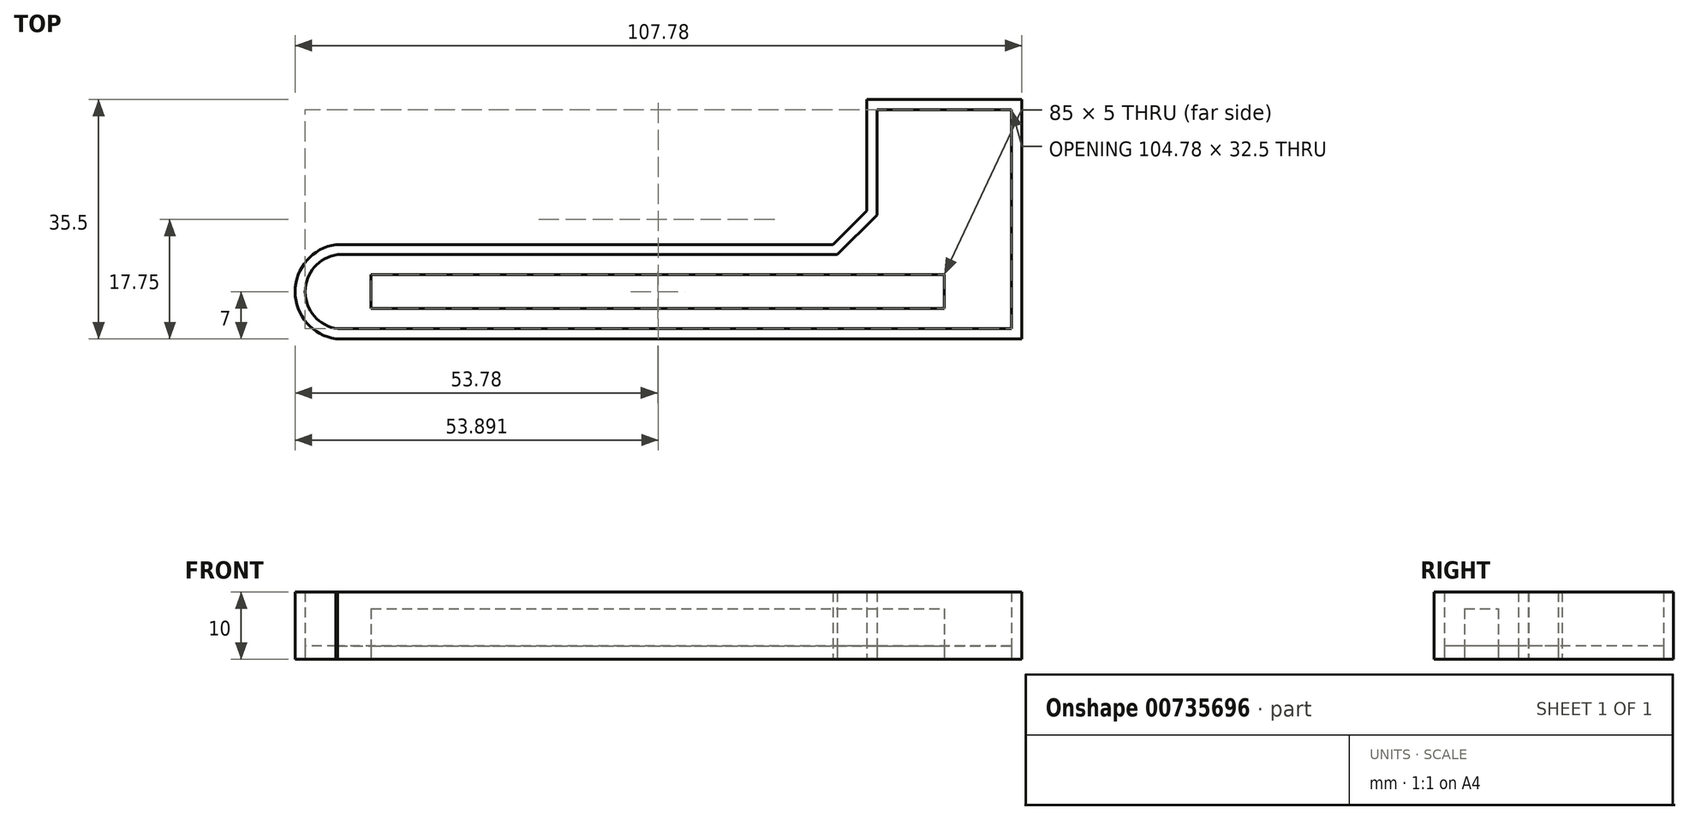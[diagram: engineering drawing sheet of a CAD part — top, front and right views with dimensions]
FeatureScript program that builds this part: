
annotation { "Feature Type Name" : "Feature", "Feature Type Description" : "" }
export const myFeature = defineFeature(function(context is Context, id is Id, definition is map)
    precondition{}
    {
        {
            var Q0;
            Q0=qCreatedBy(makeId("Top.planeOp"),FACE);
            var sketch = newSketch(context, id + "F0", { "sketchPlane" : qUnion([Q0])});
            skLineSegment(sketch, "E0", {"start": v(-133.1, 0.86) * mm, "end": v(-138.1, 0.86) * mm});
            skLineSegment(sketch, "E1", {"start": v(-133.1, 11.86) * mm, "end": v(-138.1, 11.86) * mm});
            skArc(sketch, "E2", {"start": v(-138.1, 11.86) * mm, "mid": v(-142.89, 6.36) * mm, "end": v(-138.1, 0.86) * mm});
            skArc(sketch, "E3.0", {"start": v(-138.32, 13.35) * mm, "mid": v(-144.39, 6.36) * mm, "end": v(-138.32, -0.63) * mm});
            skLineSegment(sketch, "E4", {"start": v(-138.32, 13.35) * mm, "end": v(-138.1, 13.36) * mm});
            skLineSegment(sketch, "E5", {"start": v(-138.1, -0.64) * mm, "end": v(-138.32, -0.63) * mm});
            skLineSegment(sketch, "E6", {"start": v(-48.1, 33.36) * mm, "end": v(-58.1, 33.36) * mm});
            skLineSegment(sketch, "E7", {"start": v(-58.1, 33.36) * mm, "end": v(-38.1, 33.36) * mm});
            skLineSegment(sketch, "E8.left", {"start": v(-58.1, 33.36) * mm, "end": v(-58.1, 23.36) * mm});
            skLineSegment(sketch, "E9.0", {"start": v(-59.6, 33.36) * mm, "end": v(-59.6, 23.98) * mm});
            skLineSegment(sketch, "E10.0", {"start": v(-58.1, 34.86) * mm, "end": v(-38.1, 34.86) * mm});
            skLineSegment(sketch, "E11.0", {"start": v(-36.6, 33.36) * mm, "end": v(-36.6, 23.98) * mm});
            skLineSegment(sketch, "E12", {"start": v(-59.6, 33.36) * mm, "end": v(-59.6, 34.86) * mm});
            skLineSegment(sketch, "E13", {"start": v(-59.6, 34.86) * mm, "end": v(-58.1, 34.86) * mm});
            skLineSegment(sketch, "E14", {"start": v(-38.1, 34.86) * mm, "end": v(-36.6, 34.86) * mm});
            skLineSegment(sketch, "E15", {"start": v(-36.6, 34.86) * mm, "end": v(-36.6, 33.36) * mm});
            skPoint(sketch, "E16.orphan", {"position": v(-38.1, 23.36) * mm});
            skPoint(sketch, "E8.top.start.orphan", {"position": v(-58.1, 13.36) * mm});
            skPoint(sketch, "E17.orphan", {"position": v(-38.1, 13.36) * mm});
            skLineSegment(sketch, "E18.trimOffspring", {"start": v(-69.6, 11.86) * mm, "end": v(-138.1, 11.86) * mm});
            skLineSegment(sketch, "E19.trimOffspring", {"start": v(-70.23, 13.36) * mm, "end": v(-138.1, 13.36) * mm});
            skPoint(sketch, "E20.end.orphan", {"position": v(-48.1, 13.36) * mm});
            skPoint(sketch, "E21.start.orphan", {"position": v(-48.1, 8.86) * mm});
            skLineSegment(sketch, "E22", {"start": v(-70.23, 13.36) * mm, "end": v(-64.6, 13.36) * mm});
            skLineSegment(sketch, "E23", {"start": v(-59.6, 18.36) * mm, "end": v(-59.6, 23.98) * mm});
            skLineSegment(sketch, "E24", {"start": v(-64.6, 13.36) * mm, "end": v(-64.92, 13.36) * mm});
            skLineSegment(sketch, "E25", {"start": v(-59.6, 18.36) * mm, "end": v(-64.6, 13.36) * mm});
            skLineSegment(sketch, "E26.0", {"start": v(-58.55, 17.3) * mm, "end": v(-63.55, 12.3) * mm});
            skLineSegment(sketch, "E27", {"start": v(-69.6, 11.86) * mm, "end": v(-63.99, 11.86) * mm});
            skLineSegment(sketch, "E28", {"start": v(-63.55, 12.3) * mm, "end": v(-63.99, 11.86) * mm});
            skLineSegment(sketch, "E29", {"start": v(-58.1, 23.36) * mm, "end": v(-58.1, 17.74) * mm});
            skLineSegment(sketch, "E30", {"start": v(-58.55, 17.3) * mm, "end": v(-58.1, 17.74) * mm});
            skPoint(sketch, "E31.orphan", {"position": v(-59.6, 13.36) * mm});
            skLineSegment(sketch, "E32.MirrorCS", {"start": v(-36.6, 33.36) * mm, "end": v(-36.6, 34.86) * mm});
            skLineSegment(sketch, "E33.MirrorCS", {"start": v(-36.6, 34.86) * mm, "end": v(-38.1, 34.86) * mm});
            skLineSegment(sketch, "E34.MirrorCS", {"start": v(-36.6, 18.36) * mm, "end": v(-36.6, 23.98) * mm});
            skPoint(sketch, "E35.MirrorP", {"position": v(-36.6, 13.36) * mm});
            skLineSegment(sketch, "E36", {"start": v(-137.33, 6.36) * mm, "end": v(-133.1, 6.36) * mm, "construction": true});
            skLineSegment(sketch, "E37", {"start": v(-133.1, 6.36) * mm, "end": v(-133.1, 3.86) * mm});
            skLineSegment(sketch, "E38", {"start": v(-133.1, 3.86) * mm, "end": v(-48.1, 3.86) * mm});
            skLineSegment(sketch, "E39", {"start": v(-138.1, -0.64) * mm, "end": v(-36.6, -0.64) * mm});
            skLineSegment(sketch, "E40", {"start": v(-36.6, -0.64) * mm, "end": v(-36.6, 18.36) * mm});
            skLineSegment(sketch, "E41", {"start": v(-133.1, 6.36) * mm, "end": v(-133.1, 8.86) * mm});
            skLineSegment(sketch, "E42", {"start": v(-133.1, 8.86) * mm, "end": v(-48.1, 8.86) * mm});
            skLineSegment(sketch, "E43", {"start": v(-48.1, 8.86) * mm, "end": v(-48.1, 3.86) * mm});
            skLineSegment(sketch, "E44", {"start": v(-38.1, 33.36) * mm, "end": v(-38.1, 0.86) * mm});
            skLineSegment(sketch, "E45", {"start": v(-38.1, 0.86) * mm, "end": v(-133.1, 0.86) * mm});
            skSolve(sketch);
        }
        {
            var Q0;
            Q0=makeQuery(id+"F0.imprint","IMPRINT",FACE,{"disambiguationData":[TD([[makeQuery(id+"F0.imprint","IMPRINT",EDGE,{"derivedFrom":sQuery(id+"F0.wireOp",EDGE,"E0")}),1.0]])]});
            extrude(context, id + "F1", {"entities" : qUnion([Q0]), "depth" : 10 * mm, "offsetDistance" : 25 * mm});
        }
        {
            var Q0;
            Q0=makeQuery(id+"F0.imprint","IMPRINT",FACE,{"disambiguationData":[TD([[makeQuery(id+"F0.imprint","IMPRINT",EDGE,{"derivedFrom":sQuery(id+"F0.wireOp",EDGE,"E37")}),1.0]])]});
            extrude(context, id + "F2", {"entities" : qUnion([Q0]), "depth" : 7.5 * mm, "offsetDistance" : 25 * mm});
        }
        {
            var Q0;
            Q0=makeQuery(id+"F0.imprint","IMPRINT",FACE,{"disambiguationData":[TD([[makeQuery(id+"F0.imprint","IMPRINT",EDGE,{"derivedFrom":sQuery(id+"F0.wireOp",EDGE,"E0")}),-1.0]])]});
            extrude(context, id + "F3", {"entities" : qUnion([Q0]), "depth" : 2 * mm, "offsetDistance" : 25 * mm});
        }
    });
